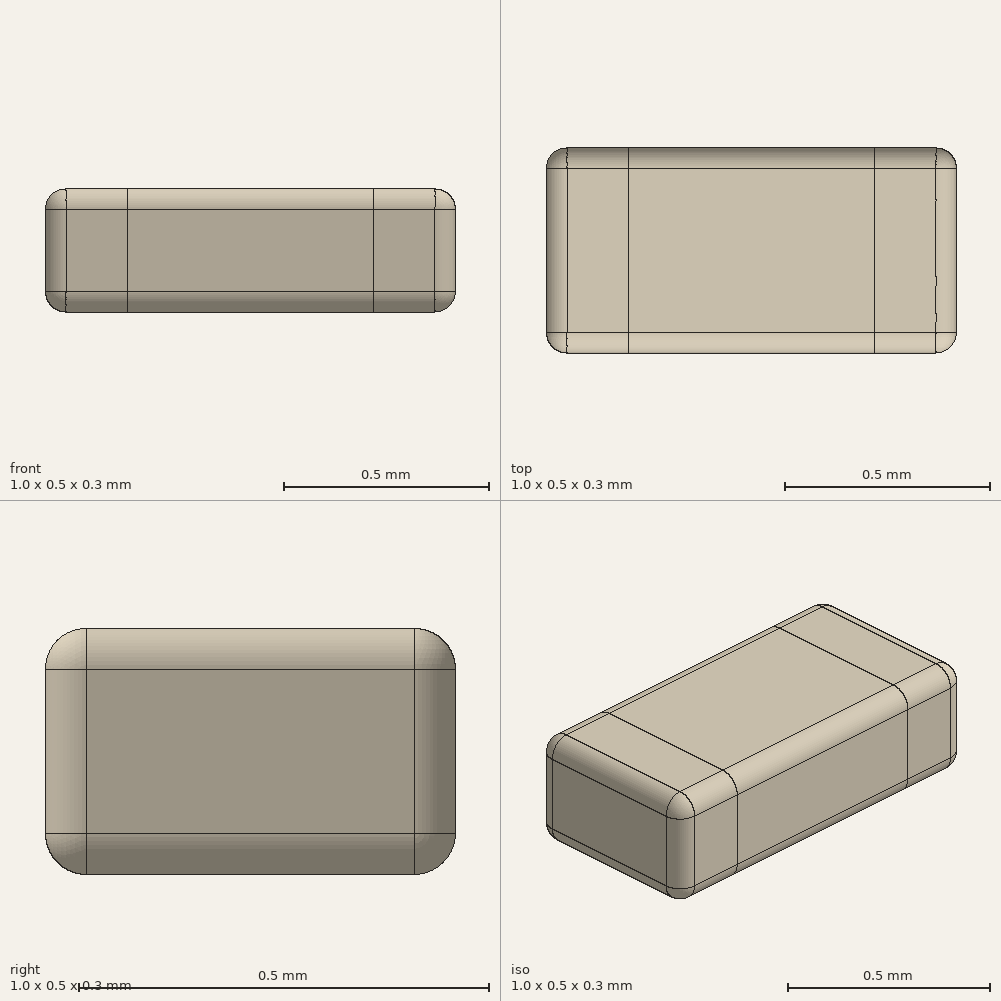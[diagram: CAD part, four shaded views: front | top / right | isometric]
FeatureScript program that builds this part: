
annotation { "Feature Type Name" : "Feature", "Feature Type Description" : "" }
export const myFeature = defineFeature(function(context is Context, id is Id, definition is map)
    precondition{}
    {
        {
            assignVariable(context, id + "F0", {"name" : "H", "anyValue" : 0.3});
        }
        {
            assignVariable(context, id + "F1", {"name" : "r", "anyValue" : 0.05});
        }
        {
            var Q0;
            Q0=qCreatedBy(makeId("Top.planeOp"),FACE);
            var sketch = newSketch(context, id + "F2", { "sketchPlane" : qUnion([Q0])});
            skLineSegment(sketch, "E0.bottom", {"start": v(0.3, 0.25) * mm, "end": v(-0.3, 0.25) * mm});
            skLineSegment(sketch, "E0.top", {"start": v(0.3, -0.25) * mm, "end": v(-0.3, -0.25) * mm});
            skLineSegment(sketch, "E0.left", {"start": v(0.3, 0.25) * mm, "end": v(0.3, -0.25) * mm});
            skLineSegment(sketch, "E0.right", {"start": v(-0.3, 0.25) * mm, "end": v(-0.3, -0.25) * mm});
            skPoint(sketch, "E0.middle", {"position": v(0, 0) * mm});
            skLineSegment(sketch, "E1", {"start": v(0.3, 0.25) * mm, "end": v(0.5, 0.25) * mm});
            skLineSegment(sketch, "E2", {"start": v(0.5, 0.25) * mm, "end": v(0.5, -0.25) * mm});
            skLineSegment(sketch, "E3", {"start": v(0.5, -0.25) * mm, "end": v(0.3, -0.25) * mm});
            skLineSegment(sketch, "E4", {"start": v(-0.3, -0.25) * mm, "end": v(-0.5, -0.25) * mm});
            skLineSegment(sketch, "E5", {"start": v(-0.5, -0.25) * mm, "end": v(-0.5, 0.25) * mm});
            skLineSegment(sketch, "E6", {"start": v(-0.5, 0.25) * mm, "end": v(-0.3, 0.25) * mm});
            skSolve(sketch);
        }
        {
            var Q0;
            Q0=makeQuery(id+"F2.imprint","IMPRINT",FACE,{"disambiguationData":[TD([[makeQuery(id+"F2.imprint","IMPRINT",EDGE,{"derivedFrom":sQuery(id+"F2.wireOp",EDGE,"E0.bottom")}),1.0]])]});
            extrude(context, id + "F3", {"entities" : qUnion([Q0]), "depth" : (getVariable(context, 'H')) * mm});
        }
        {
            var Q0;
            Q0=makeQuery(id+"F2.imprint","IMPRINT",FACE,{"disambiguationData":[TD([[makeQuery(id+"F2.imprint","IMPRINT",EDGE,{"derivedFrom":sQuery(id+"F2.wireOp",EDGE,"E0.right")}),-1.0]])]});
            extrude(context, id + "F4", {"entities" : qUnion([Q0]), "depth" : (getVariable(context, 'H')) * mm});
        }
        {
            var Q0;
            Q0=makeQuery(id+"F2.imprint","IMPRINT",FACE,{"disambiguationData":[TD([[makeQuery(id+"F2.imprint","IMPRINT",EDGE,{"derivedFrom":sQuery(id+"F2.wireOp",EDGE,"E0.left")}),1.0]])]});
            extrude(context, id + "F5", {"entities" : qUnion([Q0]), "depth" : (getVariable(context, 'H')) * mm});
        }
        {
            var Q0;
            Q0=makeQuery(id+"F4.opExtrude","CAP_EDGE",EDGE,{"disambiguationData":[OSD([sQuery(id+"F2.wireOp",EDGE,"E4")])],"isStart":false});
            var Q1;
            Q1=makeQuery(id+"F3.opExtrude","CAP_EDGE",EDGE,{"disambiguationData":[OSD([sQuery(id+"F2.wireOp",EDGE,"E0.top")])],"isStart":false});
            var Q2;
            Q2=makeQuery(id+"F5.opExtrude","CAP_EDGE",EDGE,{"disambiguationData":[OSD([sQuery(id+"F2.wireOp",EDGE,"E3")])],"isStart":false});
            var Q3;
            Q3=makeQuery(id+"F5.opExtrude","SWEPT_FACE",FACE,{"disambiguationData":[OSD([sQuery(id+"F2.wireOp",EDGE,"E2")])]});
            var Q4;
            Q4=makeQuery(id+"F5.opExtrude","CAP_EDGE",EDGE,{"disambiguationData":[OSD([sQuery(id+"F2.wireOp",EDGE,"E3")])],"isStart":true});
            var Q5;
            Q5=makeQuery(id+"F3.opExtrude","CAP_EDGE",EDGE,{"disambiguationData":[OSD([sQuery(id+"F2.wireOp",EDGE,"E0.top")])],"isStart":true});
            var Q6;
            Q6=makeQuery(id+"F4.opExtrude","CAP_EDGE",EDGE,{"disambiguationData":[OSD([sQuery(id+"F2.wireOp",EDGE,"E4")])],"isStart":true});
            var Q7;
            Q7=makeQuery(id+"F3.opExtrude","CAP_EDGE",EDGE,{"disambiguationData":[OSD([sQuery(id+"F2.wireOp",EDGE,"E0.bottom")])],"isStart":false});
            var Q8;
            Q8=makeQuery(id+"F5.opExtrude","CAP_EDGE",EDGE,{"disambiguationData":[OSD([sQuery(id+"F2.wireOp",EDGE,"E1")])],"isStart":false});
            var Q9;
            Q9=makeQuery(id+"F5.opExtrude","CAP_EDGE",EDGE,{"disambiguationData":[OSD([sQuery(id+"F2.wireOp",EDGE,"E1")])],"isStart":true});
            var Q10;
            Q10=makeQuery(id+"F4.opExtrude","SWEPT_FACE",FACE,{"disambiguationData":[OSD([sQuery(id+"F2.wireOp",EDGE,"E5")])]});
            var Q11;
            Q11=makeQuery(id+"F4.opExtrude","CAP_EDGE",EDGE,{"disambiguationData":[OSD([sQuery(id+"F2.wireOp",EDGE,"E6")])],"isStart":true});
            var Q12;
            Q12=makeQuery(id+"F3.opExtrude","CAP_EDGE",EDGE,{"disambiguationData":[OSD([sQuery(id+"F2.wireOp",EDGE,"E0.bottom")])],"isStart":true});
            var Q13;
            Q13=makeQuery(id+"F4.opExtrude","CAP_EDGE",EDGE,{"disambiguationData":[OSD([sQuery(id+"F2.wireOp",EDGE,"E6")])],"isStart":false});
            fillet(context, id + "F6", {"entities" : qUnion([Q0, Q1, Q2, Q3, Q4, Q5, Q6, Q7, Q8, Q9, Q10, Q11, Q12, Q13]), "radius" : (getVariable(context, 'r')) * mm, "tangentPropagation" : true, "allowEdgeOverflow" : false});
        }
    });
